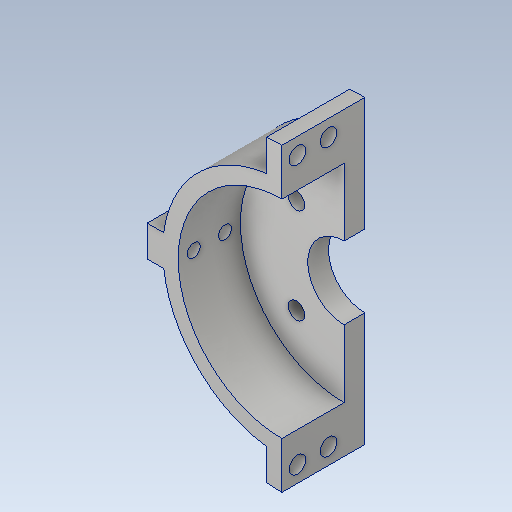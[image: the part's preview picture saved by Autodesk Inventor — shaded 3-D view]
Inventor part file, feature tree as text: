
AUTODESK INVENTOR PART (.ipt)
format: ipt  version: 2020 (Build 240168000, 168)  size: 230,912 bytes
history: native  units: mm
features: extrude x7, sketch x7, projected_geometry x5, other x1
ambient origin geometry x8: Origin, YZ Plane, XZ Plane, XY Plane, X Axis, Y Axis, Z Axis, Center Point
bodies: Body1 (feature_tree)
feature tree (20):
  other  "솔리드1"
  extrude  "돌출1"  Depth=14.0mm
  extrude  "돌출2"  Depth=46.0mm
  extrude  "돌출3"  Depth=4.0mm TaperAngle=0.0deg
  extrude  "돌출5"  Depth=40.0mm
  extrude  "돌출6"  Depth=46.0mm
  extrude  "돌출7"  Depth=29.0mm
  extrude  "돌출8"  Depth=29.0mm
  sketch  "스케치1"
  sketch  "스케치2"
  sketch  "스케치3"
  projected_geometry  "투영된 루프1"
  projected_geometry  "투영된 루프2"
  sketch  "스케치5"
  sketch  "스케치6"
  projected_geometry  "투영된 루프3"
  sketch  "스케치7"
  sketch  "스케치8"
  projected_geometry  "투영된 루프4"
  projected_geometry  "투영된 루프5"
